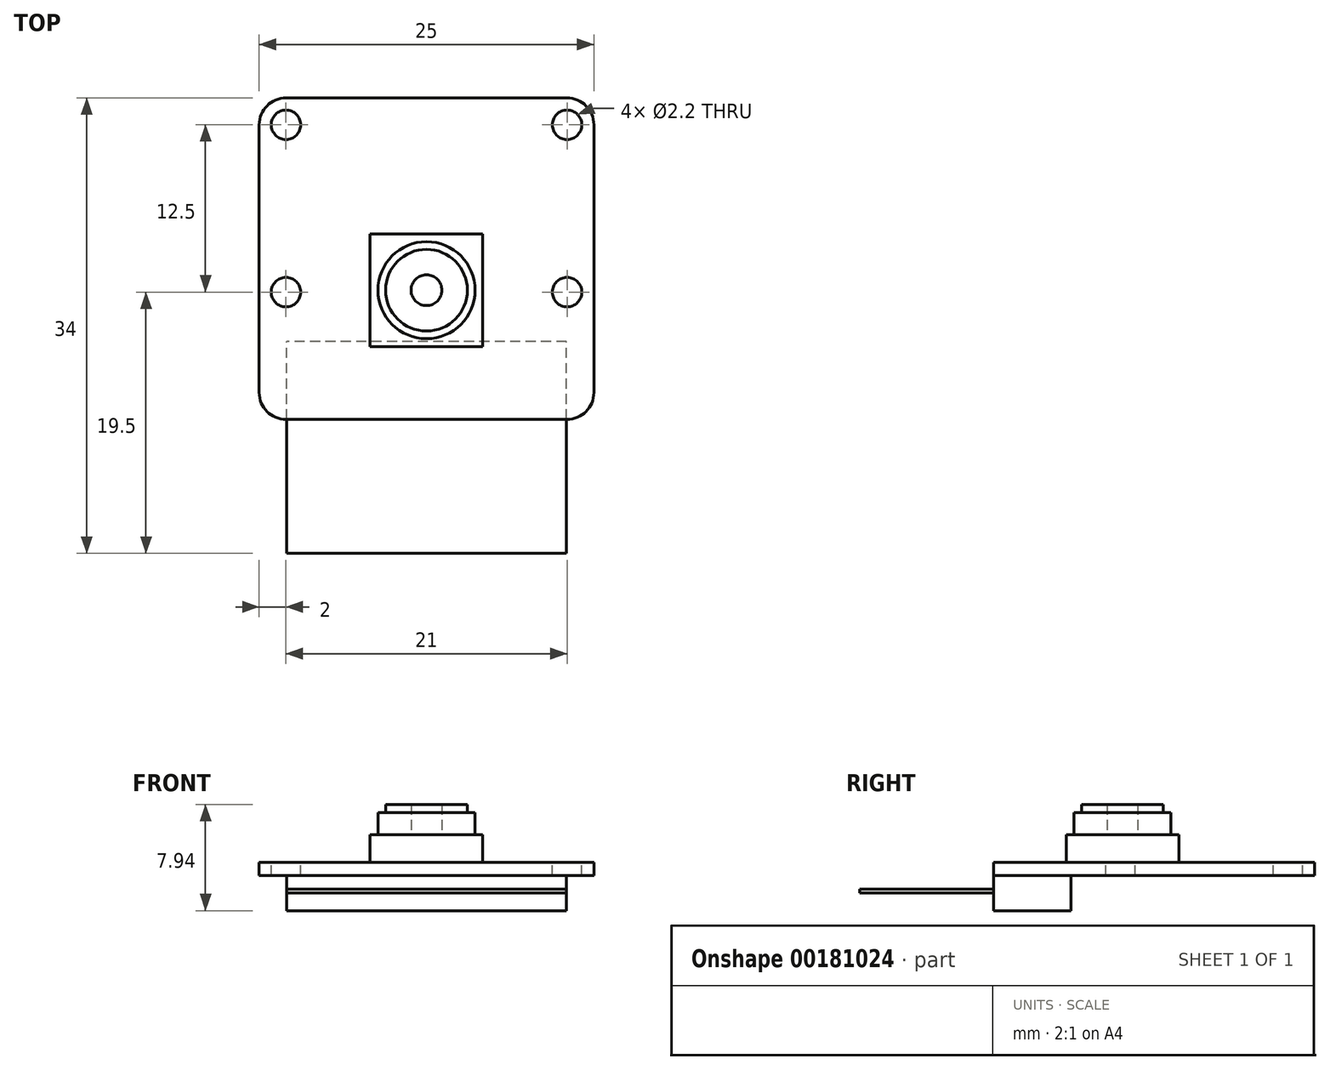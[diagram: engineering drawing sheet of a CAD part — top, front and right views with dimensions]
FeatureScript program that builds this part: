
annotation { "Feature Type Name" : "Feature", "Feature Type Description" : "" }
export const myFeature = defineFeature(function(context is Context, id is Id, definition is map)
    precondition{}
    {
        {
            var Q0;
            Q0=qCreatedBy(makeId("Top.planeOp"),FACE);
            var sketch = newSketch(context, id + "F0", { "sketchPlane" : qUnion([Q0])});
            skLineSegment(sketch, "E0.bottom", {"start": v(10.5, 12) * mm, "end": v(-10.5, 12) * mm});
            skLineSegment(sketch, "E0.top", {"start": v(10.5, -12) * mm, "end": v(-10.5, -12) * mm});
            skLineSegment(sketch, "E0.left", {"start": v(12.5, 10) * mm, "end": v(12.5, -10) * mm});
            skLineSegment(sketch, "E0.right", {"start": v(-12.5, 10) * mm, "end": v(-12.5, -10) * mm});
            skPoint(sketch, "E0.middle", {"position": v(0, 0) * mm});
            skPoint(sketch, "E1.visualSharp", {"position": v(-12.5, 12) * mm});
            skArc(sketch, "E1.filletArc", {"start": v(-10.5, 12) * mm, "mid": v(-11.91, 11.41) * mm, "end": v(-12.5, 10) * mm});
            skPoint(sketch, "E2.visualSharp", {"position": v(12.5, 12) * mm});
            skArc(sketch, "E2.filletArc", {"start": v(12.5, 10) * mm, "mid": v(11.91, 11.41) * mm, "end": v(10.5, 12) * mm});
            skPoint(sketch, "E3.visualSharp", {"position": v(12.5, -12) * mm});
            skArc(sketch, "E3.filletArc", {"start": v(10.5, -12) * mm, "mid": v(11.91, -11.41) * mm, "end": v(12.5, -10) * mm});
            skPoint(sketch, "E4.visualSharp", {"position": v(-12.5, -12) * mm});
            skArc(sketch, "E4.filletArc", {"start": v(-12.5, -10) * mm, "mid": v(-11.91, -11.41) * mm, "end": v(-10.5, -12) * mm});
            skSolve(sketch);
        }
        {
            var Q0;
            Q0=makeQuery(id+"F0.imprint","IMPRINT",FACE,{"disambiguationData":[TD([[makeQuery(id+"F0.imprint","IMPRINT",EDGE,{"derivedFrom":sQuery(id+"F0.wireOp",EDGE,"E0.bottom")}),1.0]])]});
            extrude(context, id + "F1", {"entities" : qUnion([Q0]), "oppositeDirection" : true, "depth" : 1 * mm});
        }
        {
            var Q0;
            Q0=makeQuery(id+"F1.opExtrude","CAP_FACE",FACE,{"disambiguationData":[OSD([sQuery(id+"F0.wireOp",EDGE,"E0.bottom"),sQuery(id+"F0.wireOp",EDGE,"E0.top"),sQuery(id+"F0.wireOp",EDGE,"E0.left"),sQuery(id+"F0.wireOp",EDGE,"E0.right"),sQuery(id+"F0.wireOp",EDGE,"E1.filletArc"),sQuery(id+"F0.wireOp",EDGE,"E2.filletArc"),sQuery(id+"F0.wireOp",EDGE,"E3.filletArc"),sQuery(id+"F0.wireOp",EDGE,"E4.filletArc")])],"isStart":true});
            var sketch = newSketch(context, id + "F2", { "sketchPlane" : qUnion([Q0])});
            skCircle(sketch, "E5", {"center": v(-10.5, 10) * mm, "radius": 1.1 * mm});
            skCircle(sketch, "E6", {"center": v(-10.5, -2.5) * mm, "radius": 1.1 * mm});
            skCircle(sketch, "E7.MirrorC", {"center": v(10.5, -2.5) * mm, "radius": 1.1 * mm});
            skCircle(sketch, "E8.MirrorC", {"center": v(10.5, 10) * mm, "radius": 1.1 * mm});
            skSolve(sketch);
        }
        {
            var Q0;
            Q0 = qSketchRegion(id + "F2", true);
            extrude(context, id + "F3", {"entities" : qUnion([Q0]), "operationType" : NewBodyOperationType.REMOVE, "endBound" : BoundingType.UP_TO_NEXT, "oppositeDirection" : true, "depth" : 25 * mm});
        }
        {
            var Q0;
            Q0=makeQuery(id+"F1.opExtrude","CAP_FACE",FACE,{"disambiguationData":[OSD([sQuery(id+"F0.wireOp",EDGE,"E0.bottom"),sQuery(id+"F0.wireOp",EDGE,"E0.top"),sQuery(id+"F0.wireOp",EDGE,"E0.left"),sQuery(id+"F0.wireOp",EDGE,"E0.right"),sQuery(id+"F0.wireOp",EDGE,"E1.filletArc"),sQuery(id+"F0.wireOp",EDGE,"E2.filletArc"),sQuery(id+"F0.wireOp",EDGE,"E3.filletArc"),sQuery(id+"F0.wireOp",EDGE,"E4.filletArc")])],"isStart":true});
            var sketch = newSketch(context, id + "F4", { "sketchPlane" : qUnion([Q0])});
            skLineSegment(sketch, "E9.bottom", {"start": v(4.2, 1.85) * mm, "end": v(-4.2, 1.85) * mm});
            skLineSegment(sketch, "E9.top", {"start": v(4.2, -6.56) * mm, "end": v(-4.2, -6.56) * mm});
            skLineSegment(sketch, "E9.left", {"start": v(4.2, 1.85) * mm, "end": v(4.2, -6.56) * mm});
            skLineSegment(sketch, "E9.right", {"start": v(-4.2, 1.85) * mm, "end": v(-4.2, -6.56) * mm});
            skPoint(sketch, "E9.middle", {"position": v(0, -2.36) * mm});
            skSolve(sketch);
        }
        {
            var Q0;
            Q0 = qSketchRegion(id + "F4", true);
            extrude(context, id + "F5", {"entities" : qUnion([Q0]), "depth" : 2.05 * mm});
        }
        {
            var Q0;
            Q0=makeQuery(id+"F5.opExtrude","CAP_FACE",FACE,{"disambiguationData":[OSD([sQuery(id+"F4.wireOp",EDGE,"E9.bottom"),sQuery(id+"F4.wireOp",EDGE,"E9.top"),sQuery(id+"F4.wireOp",EDGE,"E9.left"),sQuery(id+"F4.wireOp",EDGE,"E9.right")])],"isStart":false});
            var sketch = newSketch(context, id + "F6", { "sketchPlane" : qUnion([Q0])});
            skCircle(sketch, "E10", {"center": v(0, -2.36) * mm, "radius": 3.62 * mm});
            skLineSegment(sketch, "E11", {"start": v(0, 1.85) * mm, "end": v(0, -6.56) * mm, "construction": true});
            skLineSegment(sketch, "E12", {"start": v(-4.2, -2.36) * mm, "end": v(4.2, -2.36) * mm, "construction": true});
            skCircle(sketch, "E13", {"center": v(0, -2.36) * mm, "radius": 3.05 * mm});
            skCircle(sketch, "E14", {"center": v(0, -2.36) * mm, "radius": 1.15 * mm});
            skSolve(sketch);
        }
        {
            var Q0;
            Q0 = qSketchRegion(id + "F6", true);
            var Q1;
            Q1=makeQuery(id+"F6.imprint","IMPRINT",FACE,{"disambiguationData":[TD([[makeQuery(id+"F6.imprint","IMPRINT",EDGE,{"derivedFrom":sQuery(id+"F6.wireOp",EDGE,"E13")}),1.0]])]});
            var Q2;
            Q2=makeQuery(id+"F6.imprint","IMPRINT",FACE,{"disambiguationData":[TD([[makeQuery(id+"F6.imprint","IMPRINT",EDGE,{"derivedFrom":sQuery(id+"F6.wireOp",EDGE,"E14")}),1.0]])]});
            extrude(context, id + "F7", {"entities" : qUnion([Q0, Q1, Q2]), "operationType" : NewBodyOperationType.ADD, "depth" : 1.65 * mm});
        }
        {
            var Q0;
            Q0=makeQuery(id+"F6.imprint","IMPRINT",FACE,{"disambiguationData":[TD([[makeQuery(id+"F6.imprint","IMPRINT",EDGE,{"derivedFrom":sQuery(id+"F6.wireOp",EDGE,"E13")}),1.0]])]});
            var Q1;
            Q1=makeQuery(id+"F6.imprint","IMPRINT",FACE,{"disambiguationData":[TD([[makeQuery(id+"F6.imprint","IMPRINT",EDGE,{"derivedFrom":sQuery(id+"F6.wireOp",EDGE,"E14")}),1.0]])]});
            extrude(context, id + "F8", {"entities" : qUnion([Q0, Q1]), "operationType" : NewBodyOperationType.ADD, "depth" : 2.25 * mm});
        }
        {
            var Q0;
            Q0=makeQuery(id+"F6.imprint","IMPRINT",FACE,{"disambiguationData":[TD([[makeQuery(id+"F6.imprint","IMPRINT",EDGE,{"derivedFrom":sQuery(id+"F6.wireOp",EDGE,"E14")}),1.0]])]});
            extrude(context, id + "F9", {"entities" : qUnion([Q0]), "depth" : 2.27 * mm});
        }
        {
            var Q0;
            Q0=makeQuery(id+"F1.opExtrude","CAP_FACE",FACE,{"disambiguationData":[OSD([sQuery(id+"F0.wireOp",EDGE,"E0.bottom"),sQuery(id+"F0.wireOp",EDGE,"E0.top"),sQuery(id+"F0.wireOp",EDGE,"E0.left"),sQuery(id+"F0.wireOp",EDGE,"E0.right"),sQuery(id+"F0.wireOp",EDGE,"E1.filletArc"),sQuery(id+"F0.wireOp",EDGE,"E2.filletArc"),sQuery(id+"F0.wireOp",EDGE,"E3.filletArc"),sQuery(id+"F0.wireOp",EDGE,"E4.filletArc")])],"isStart":false});
            var sketch = newSketch(context, id + "F10", { "sketchPlane" : qUnion([Q0])});
            skLineSegment(sketch, "E15.bottom", {"start": v(10.45, 12) * mm, "end": v(-10.45, 12) * mm});
            skLineSegment(sketch, "E15.top", {"start": v(10.45, 6.2) * mm, "end": v(-10.45, 6.2) * mm});
            skLineSegment(sketch, "E15.left", {"start": v(10.45, 12) * mm, "end": v(10.45, 6.2) * mm});
            skLineSegment(sketch, "E15.right", {"start": v(-10.45, 12) * mm, "end": v(-10.45, 6.2) * mm});
            skPoint(sketch, "E15.middle", {"position": v(0, 9.1) * mm});
            skSolve(sketch);
        }
        {
            var Q0;
            Q0 = qSketchRegion(id + "F10", true);
            extrude(context, id + "F11", {"entities" : qUnion([Q0]), "depth" : 2.62 * mm});
        }
        {
            var Q0;
            Q0=makeQuery(id+"F11.boolean.opBoolean","MERGE",FACE,{"derivedFrom":[makeQuery(id+"F1.opExtrude","SWEPT_FACE",FACE,{"disambiguationData":[OSD([sQuery(id+"F0.wireOp",EDGE,"E0.top")])]}),makeQuery(id+"F11.opExtrude","SWEPT_FACE",FACE,{"disambiguationData":[OSD([sQuery(id+"F10.wireOp",EDGE,"E15.bottom")])]})]});
            var sketch = newSketch(context, id + "F12", { "sketchPlane" : qUnion([Q0])});
            skLineSegment(sketch, "E16.bottom", {"start": v(-10.45, -2) * mm, "end": v(10.45, -2) * mm});
            skLineSegment(sketch, "E16.top", {"start": v(-10.45, -2.31) * mm, "end": v(10.45, -2.31) * mm});
            skLineSegment(sketch, "E16.left", {"start": v(-10.45, -2) * mm, "end": v(-10.45, -2.31) * mm});
            skLineSegment(sketch, "E16.right", {"start": v(10.45, -2) * mm, "end": v(10.45, -2.31) * mm});
            skSolve(sketch);
        }
        {
            var Q0;
            Q0 = qSketchRegion(id + "F12", true);
            extrude(context, id + "F13", {"entities" : qUnion([Q0]), "depth" : 10 * mm});
        }
    });
